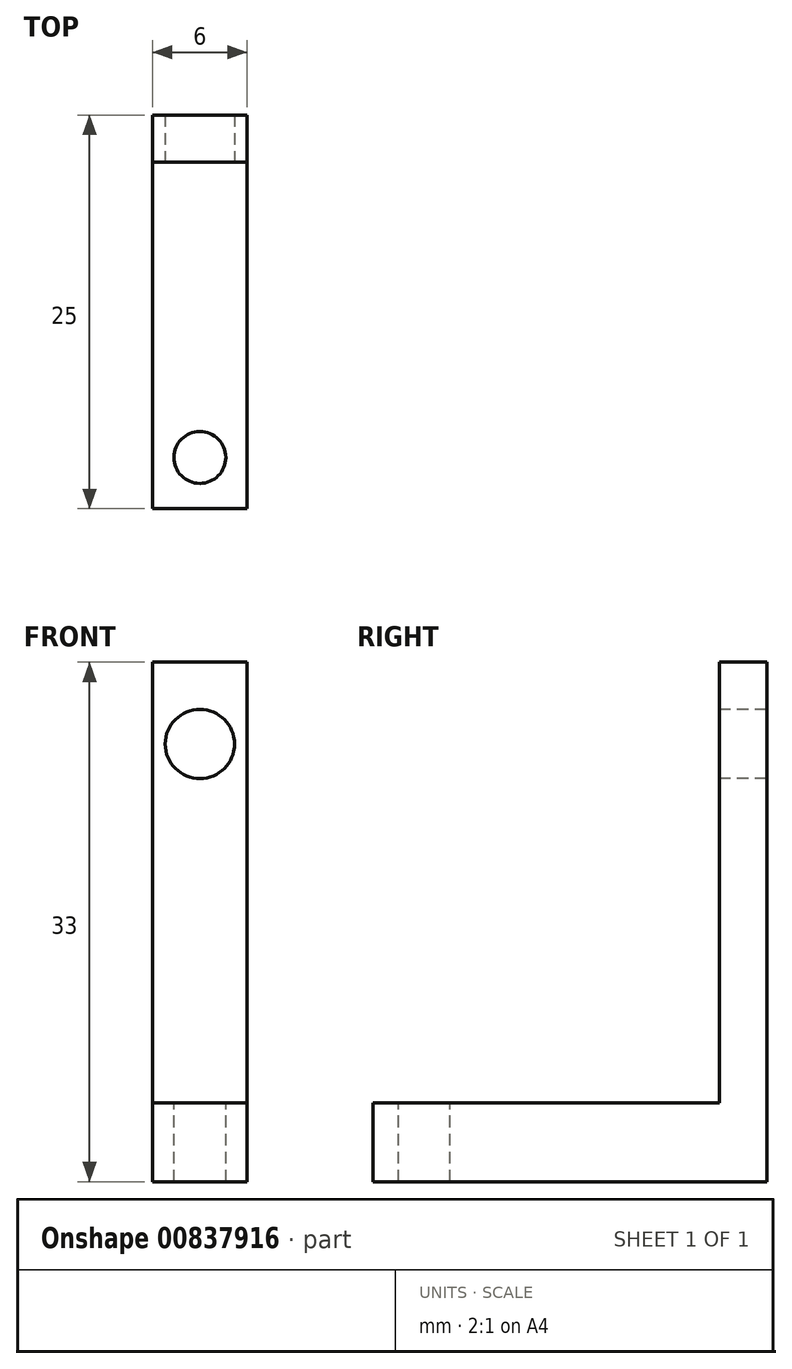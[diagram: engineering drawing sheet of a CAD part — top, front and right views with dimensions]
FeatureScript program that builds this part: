
annotation { "Feature Type Name" : "Feature", "Feature Type Description" : "" }
export const myFeature = defineFeature(function(context is Context, id is Id, definition is map)
    precondition{}
    {
        {
            var Q0;
            Q0=qCreatedBy(makeId("Top.planeOp"),FACE);
            var sketch = newSketch(context, id + "F0", { "sketchPlane" : qUnion([Q0])});
            skLineSegment(sketch, "E0.bottom", {"start": v(-5.48, 7.06) * mm, "end": v(0.52, 7.06) * mm});
            skLineSegment(sketch, "E0.top", {"start": v(-5.48, -14.94) * mm, "end": v(0.52, -14.94) * mm});
            skLineSegment(sketch, "E0.left", {"start": v(-5.48, 7.06) * mm, "end": v(-5.48, -14.94) * mm});
            skLineSegment(sketch, "E0.right", {"start": v(0.52, 7.06) * mm, "end": v(0.52, -14.94) * mm});
            skSolve(sketch);
        }
        {
            var Q0;
            Q0=makeQuery(id+"F0.imprint","IMPRINT",FACE,{"disambiguationData":[TD([[makeQuery(id+"F0.imprint","IMPRINT",EDGE,{"derivedFrom":sQuery(id+"F0.wireOp",EDGE,"E0.bottom")}),-1.0]])]});
            extrude(context, id + "F1", {"entities" : qUnion([Q0]), "depth" : 5 * mm, "offsetDistance" : 25 * mm});
        }
        {
            var Q0;
            Q0=makeQuery(id+"F1.opExtrude","SWEPT_FACE",FACE,{"disambiguationData":[OSD([sQuery(id+"F0.wireOp",EDGE,"E0.left")])]});
            var sketch = newSketch(context, id + "F2", { "sketchPlane" : qUnion([Q0])});
            skLineSegment(sketch, "E1.bottom", {"start": v(-7.06, 0) * mm, "end": v(-10.06, 0) * mm});
            skLineSegment(sketch, "E1.top", {"start": v(-7.06, 33) * mm, "end": v(-10.06, 33) * mm});
            skLineSegment(sketch, "E1.left", {"start": v(-7.06, 0) * mm, "end": v(-7.06, 33) * mm});
            skLineSegment(sketch, "E1.right", {"start": v(-10.06, 0) * mm, "end": v(-10.06, 33) * mm});
            skSolve(sketch);
        }
        {
            var Q0;
            {var subQ1=sQuery(id+"F2.wireOp",EDGE,"E1.bottom");Q0=makeQuery(id+"F2.imprint","IMPRINT",FACE,{"disambiguationData":[TD([[makeQuery(id+"F2.imprint","IMPRINT",EDGE,{"derivedFrom":subQ1}),-1.0]])]});}
            extrude(context, id + "F3", {"entities" : qUnion([Q0]), "operationType" : NewBodyOperationType.ADD, "oppositeDirection" : true, "depth" : 6 * mm, "offsetDistance" : 25 * mm});
        }
        {
            var Q0;
            Q0=makeQuery(id+"F1.opExtrude","CAP_FACE",FACE,{"disambiguationData":[OSD([sQuery(id+"F0.wireOp",EDGE,"E0.bottom"),sQuery(id+"F0.wireOp",EDGE,"E0.top"),sQuery(id+"F0.wireOp",EDGE,"E0.left"),sQuery(id+"F0.wireOp",EDGE,"E0.right")])],"isStart":false});
            var sketch = newSketch(context, id + "F4", { "sketchPlane" : qUnion([Q0])});
            skPoint(sketch, "E2", {"position": v(-2.48, -11.69) * mm});
            skPoint(sketch, "E2.positionSnap0", {"position": v(-2.48, 7.06) * mm});
            skSolve(sketch);
        }
        {
            var Q0;
            Q0=sQuery(id+"F4.wireOp",VERTEX,"E2");
            var Q1;
            Q1=makeQuery(id+"F1.opExtrude","SWEPT_BODY",BODY,{"disambiguationData":[OSD([sQuery(id+"F0.wireOp",EDGE,"E0.bottom"),sQuery(id+"F0.wireOp",EDGE,"E0.top"),sQuery(id+"F0.wireOp",EDGE,"E0.left"),sQuery(id+"F0.wireOp",EDGE,"E0.right")])]});
            hole(context, id + "F5", {"style" : HoleStyle.SIMPLE, "endStyle" : HoleEndStyle.THROUGH, "standardTappedOrClearance" : lookupTablePath({ "fit" : "Normal", "standard" : "ISO", "size" : "M3", "type" : "Clearance" }), "standardBlindInLast" : lookupTablePath({ "fit" : "Standard", "standard" : "ISO", "size" : "M3", "type" : "Clearance" }), "holeDiameter" : 3.3 * mm, "majorDiameter" : 5 * mm, "isTappedThrough" : true, "tappedDepth" : 12 * mm, "tapClearance" : 3, "locations" : qUnion([Q0]), "scope" : qUnion([Q1])});
        }
        {
            var Q0;
            Q0=makeQuery(id+"F3.opExtrude","SWEPT_FACE",FACE,{"disambiguationData":[OSD([sQuery(id+"F2.wireOp",EDGE,"E1.left")])]});
            var sketch = newSketch(context, id + "F6", { "sketchPlane" : qUnion([Q0])});
            skPoint(sketch, "E3", {"position": v(-2.48, 27.8) * mm});
            skPoint(sketch, "E3.positionSnap0", {"position": v(-2.48, 33) * mm});
            skSolve(sketch);
        }
        {
            var Q0;
            Q0=sQuery(id+"F6.wireOp",VERTEX,"E3");
            var Q1;
            Q1=makeQuery(id+"F1.opExtrude","SWEPT_BODY",BODY,{"disambiguationData":[OSD([sQuery(id+"F0.wireOp",EDGE,"E0.bottom"),sQuery(id+"F0.wireOp",EDGE,"E0.top"),sQuery(id+"F0.wireOp",EDGE,"E0.left"),sQuery(id+"F0.wireOp",EDGE,"E0.right")])]});
            hole(context, id + "F7", {"style" : HoleStyle.SIMPLE, "endStyle" : HoleEndStyle.THROUGH, "standardTappedOrClearance" : lookupTablePath({ "fit" : "Normal", "standard" : "ISO", "size" : "M4", "type" : "Clearance" }), "standardBlindInLast" : lookupTablePath({ "fit" : "Standard", "standard" : "ISO", "size" : "M4", "type" : "Clearance" }), "holeDiameter" : 4.4 * mm, "majorDiameter" : 5 * mm, "isTappedThrough" : true, "tappedDepth" : 12 * mm, "tapClearance" : 3, "locations" : qUnion([Q0]), "scope" : qUnion([Q1])});
        }
    });
